# Revit family: Шкаф антивандальный настенный ШАН-М 19” 600x450
name_source: partatom
category: Обобщенные модели
units: mm (PartAtom-declared; Revit-internal decimal feet)

## family parameters
Всегда вертикально = Да
Может служить основой для арматурных стержней = Нет
На основе рабочей плоскости = Нет
Общий = Нет
При загрузке вырезать с полостями = Нет
Размер круглого соединителя = Использовать диаметр
Тип детали = Нормальный
Точка расчета площади = Нет

## types (6) — shared parameters
ADSK_URL документации изделия = https://www.ssd.ru
ADSK_URL страницы изделия = https://www.ssd.ru
ADSK_Единица измерения = шт.
ADSK_Завод-изготовитель = АО СВЯЗЬСТРОЙДЕТАЛЬ
ADSK_Количество = 1
ADSK_Материал обозначение = Серый RAL 7035
ADSK_Размер_Глубина = 450 мм
ADSK_Размер_Ширина = 600 мм

## per-type parameters (varying)
| type | ADSK_Код изделия | ADSK_Масса_Текст | ADSK_Обозначение | ADSK_Размер_Высота | Высота заклепок |
| Шкаф антивандальный настенный ШАН-М 19",6U(600*450) ССД | 130411-00463 | 23,0 | ШАН-М 6U (600х450мм) | 380 мм | 381 мм |
| Шкаф антивандальный настенный ШАН-М 19",9U(600*450) ССД | 130411-00464 | 27,0 | ШАН-М 9U (600х450мм) | 513 мм | 514 мм |
| Шкаф антивандальный настенный ШАН-М 19",12U(600*450) ССД | 130411-00465 | 31,7 | ШАН-М 12U (600х450мм) | 647 мм | 648 мм |
| Шкаф антивандальный настенный ШАН-М 19",15U(600*450) ССД | 130411-00466 | 36,0 | ШАН-М 15U (600х450мм) | 780 мм | 781 мм |
| Шкаф антивандальный настенный ШАН-М 19",18U(600*450) ССД | 130411-00467 | 41,0 | ШАН-М 18U (600х450мм) | 914 мм | 915 мм |
| Шкаф антивандальный настенный ШАН-М 19",22U(600*450) ССД | 130411-00468 | 47,3 | ШАН-М 22U (600х450мм) | 1092 мм | 1093 мм |

note: column(s) folded — value = type name in every type: ADSK_Наименование
